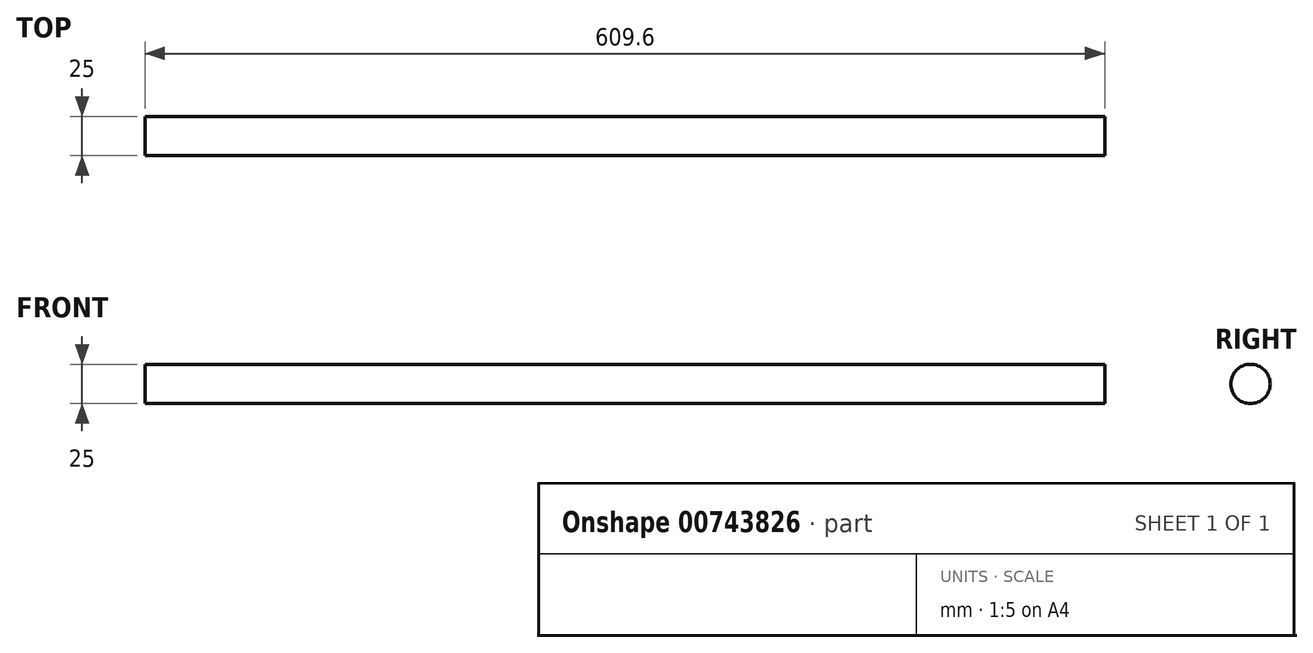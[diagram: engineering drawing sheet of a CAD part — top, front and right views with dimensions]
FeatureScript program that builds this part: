
annotation { "Feature Type Name" : "Feature", "Feature Type Description" : "" }
export const myFeature = defineFeature(function(context is Context, id is Id, definition is map)
    precondition{}
    {
        {
            var Q0;
            Q0=qCreatedBy(makeId("Right.planeOp"),FACE);
            var sketch = newSketch(context, id + "F0", { "sketchPlane" : qUnion([Q0])});
            skCircle(sketch, "E0", {"center": v(0, 0) * mm, "radius": 12.5 * mm});
            skSolve(sketch);
        }
        {
            var Q0;
            Q0=makeQuery(id+"F0.imprint","IMPRINT",FACE,{"disambiguationData":[TD([[makeQuery(id+"F0.imprint","IMPRINT",EDGE,{"derivedFrom":sQuery(id+"F0.wireOp",EDGE,"E0")}),1.0]])]});
            extrude(context, id + "F1", {"entities" : qUnion([Q0]), "endBound" : BoundingType.SYMMETRIC, "depth" : 609.6 * mm, "offsetDistance" : 25.4 * mm});
        }
    });
